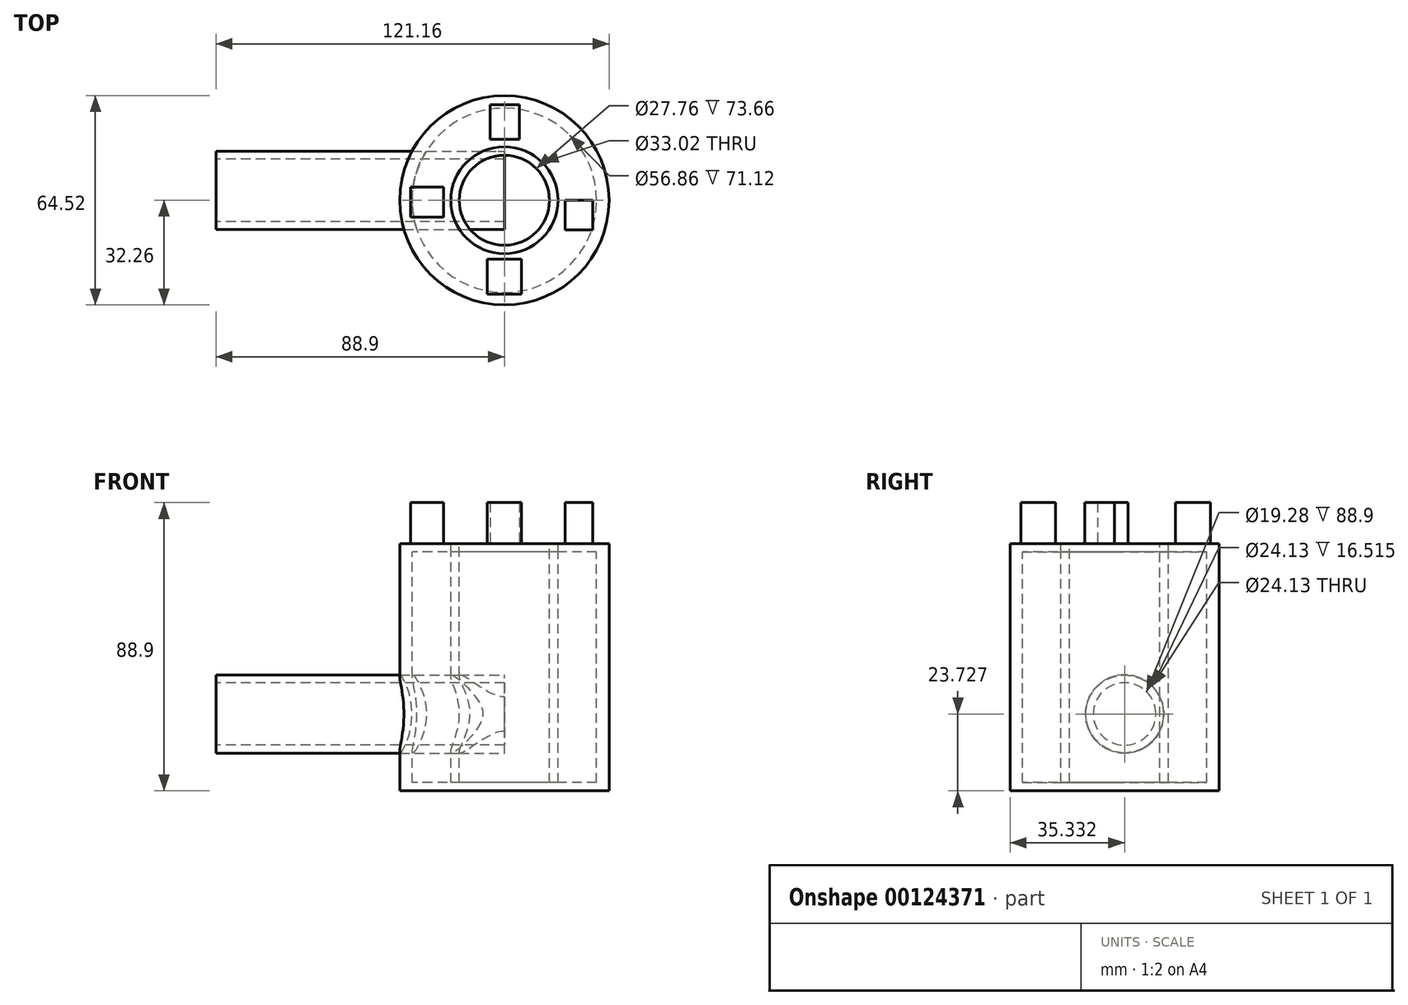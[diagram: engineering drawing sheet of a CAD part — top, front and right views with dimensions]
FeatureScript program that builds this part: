
annotation { "Feature Type Name" : "Feature", "Feature Type Description" : "" }
export const myFeature = defineFeature(function(context is Context, id is Id, definition is map)
    precondition{}
    {
        {
            var Q0;
            Q0=qCreatedBy(makeId("Top.planeOp"),FACE);
            var sketch = newSketch(context, id + "F0", { "sketchPlane" : qUnion([Q0])});
            skCircle(sketch, "E0", {"center": v(0, 0) * mm, "radius": 32.26 * mm});
            skSolve(sketch);
        }
        {
            var Q0;
            Q0=makeQuery(id+"F0.imprint","IMPRINT",FACE,{"disambiguationData":[TD([[makeQuery(id+"F0.imprint","IMPRINT",EDGE,{"derivedFrom":sQuery(id+"F0.wireOp",EDGE,"E0")}),1.0]])]});
            extrude(context, id + "F1", {"entities" : qUnion([Q0]), "depth" : 76.2 * mm});
        }
        {
            var Q0;
            Q0=makeQuery(id+"F1.opExtrude","CAP_FACE",FACE,{"disambiguationData":[OSD([sQuery(id+"F0.wireOp",EDGE,"E0")])],"isStart":false});
            var sketch = newSketch(context, id + "F2", { "sketchPlane" : qUnion([Q0])});
            skCircle(sketch, "E1", {"center": v(0, 0) * mm, "radius": 28.43 * mm});
            skSolve(sketch);
        }
        {
            var Q0;
            Q0=makeQuery(id+"F2.imprint","IMPRINT",FACE,{"disambiguationData":[TD([[makeQuery(id+"F2.imprint","IMPRINT",EDGE,{"derivedFrom":sQuery(id+"F2.wireOp",EDGE,"E1")}),1.0]])]});
            extrude(context, id + "F3", {"entities" : qUnion([Q0]), "operationType" : NewBodyOperationType.REMOVE, "oppositeDirection" : true, "depth" : 73.66 * mm});
        }
        {
            var Q0;
            Q0=makeQuery(id+"F1.opExtrude","CAP_FACE",FACE,{"disambiguationData":[OSD([sQuery(id+"F0.wireOp",EDGE,"E0")])],"isStart":false});
            var sketch = newSketch(context, id + "F4", { "sketchPlane" : qUnion([Q0])});
            skCircle(sketch, "E2", {"center": v(0, 0) * mm, "radius": 16.51 * mm});
            skCircle(sketch, "E3", {"center": v(0, 0) * mm, "radius": 28.68 * mm});
            skSolve(sketch);
        }
        {
            var Q0;
            Q0=makeQuery(id+"F4.imprint","IMPRINT",FACE,{"disambiguationData":[TD([[makeQuery(id+"F4.imprint","IMPRINT",EDGE,{"derivedFrom":sQuery(id+"F4.wireOp",EDGE,"E2")}),-1.0]])]});
            extrude(context, id + "F5", {"entities" : qUnion([Q0]), "operationType" : NewBodyOperationType.ADD, "oppositeDirection" : true, "depth" : 2.54 * mm});
        }
        {
            var Q0;
            Q0=makeQuery(id+"F5.boolean.opBoolean","MERGE",FACE,{"derivedFrom":[makeQuery(id+"F1.opExtrude","CAP_FACE",FACE,{"disambiguationData":[OSD([sQuery(id+"F0.wireOp",EDGE,"E0")])],"isStart":false}),makeQuery(id+"F5.opExtrude","CAP_FACE",FACE,{"disambiguationData":[OSD([sQuery(id+"F2.wireOp",EDGE,"E1"),sQuery(id+"F4.wireOp",EDGE,"E2")])],"isStart":true})]});
            var sketch = newSketch(context, id + "F6", { "sketchPlane" : qUnion([Q0])});
            skCircle(sketch, "E4", {"center": v(0, 0) * mm, "radius": 16.51 * mm});
            skSolve(sketch);
        }
        {
            var Q0;
            Q0 = qSketchRegion(id + "F6", true);
            extrude(context, id + "F7", {"entities" : qUnion([Q0]), "oppositeDirection" : true, "depth" : 73.66 * mm});
        }
        {
            var Q0;
            Q0=makeQuery(id+"F7.opExtrude","CAP_FACE",FACE,{"disambiguationData":[OSD([sQuery(id+"F6.wireOp",EDGE,"E4")])],"isStart":true});
            var sketch = newSketch(context, id + "F8", { "sketchPlane" : qUnion([Q0])});
            skCircle(sketch, "E5", {"center": v(0, 0) * mm, "radius": 13.88 * mm});
            skSolve(sketch);
        }
        {
            var Q0;
            Q0 = qSketchRegion(id + "F8", true);
            extrude(context, id + "F9", {"entities" : qUnion([Q0]), "operationType" : NewBodyOperationType.REMOVE, "oppositeDirection" : true, "depth" : 73.66 * mm});
        }
        {
            var Q0;
            Q0=qCreatedBy(makeId("Right.planeOp"),FACE);
            var sketch = newSketch(context, id + "F10", { "sketchPlane" : qUnion([Q0])});
            skCircle(sketch, "E6", {"center": v(3.07, 23.73) * mm, "radius": 12.07 * mm});
            skSolve(sketch);
        }
        {
            var Q0;
            Q0 = qSketchRegion(id + "F10", true);
            extrude(context, id + "F11", {"entities" : qUnion([Q0]), "operationType" : NewBodyOperationType.REMOVE, "oppositeDirection" : true, "depth" : 88.3 * mm});
        }
        {
            var Q0;
            Q0=makeQuery(id+"F5.boolean.opBoolean","MERGE",FACE,{"derivedFrom":[makeQuery(id+"F1.opExtrude","CAP_FACE",FACE,{"disambiguationData":[OSD([sQuery(id+"F0.wireOp",EDGE,"E0")])],"isStart":false}),makeQuery(id+"F5.opExtrude","CAP_FACE",FACE,{"disambiguationData":[OSD([sQuery(id+"F2.wireOp",EDGE,"E1"),sQuery(id+"F4.wireOp",EDGE,"E2")])],"isStart":true})]});
            var sketch = newSketch(context, id + "F12", { "sketchPlane" : qUnion([Q0])});
            skLineSegment(sketch, "E7.bottom", {"start": v(-4.37, 29.5) * mm, "end": v(4.66, 29.5) * mm});
            skLineSegment(sketch, "E7.top", {"start": v(-4.37, 18.77) * mm, "end": v(4.66, 18.77) * mm});
            skLineSegment(sketch, "E7.left", {"start": v(-4.37, 29.5) * mm, "end": v(-4.37, 18.77) * mm});
            skLineSegment(sketch, "E7.right", {"start": v(4.66, 29.5) * mm, "end": v(4.66, 18.77) * mm});
            skLineSegment(sketch, "E8.bottom", {"start": v(18.77, 0) * mm, "end": v(27.23, 0) * mm});
            skLineSegment(sketch, "E8.top", {"start": v(18.77, -9.17) * mm, "end": v(27.23, -9.17) * mm});
            skLineSegment(sketch, "E8.left", {"start": v(18.77, 0) * mm, "end": v(18.77, -9.17) * mm});
            skLineSegment(sketch, "E8.right", {"start": v(27.23, 0) * mm, "end": v(27.23, -9.17) * mm});
            skLineSegment(sketch, "E9.bottom", {"start": v(-5.22, -18.2) * mm, "end": v(5.22, -18.2) * mm});
            skLineSegment(sketch, "E9.top", {"start": v(-5.22, -28.93) * mm, "end": v(5.22, -28.93) * mm});
            skLineSegment(sketch, "E9.left", {"start": v(-5.22, -18.2) * mm, "end": v(-5.22, -28.93) * mm});
            skLineSegment(sketch, "E9.right", {"start": v(5.22, -18.2) * mm, "end": v(5.22, -28.93) * mm});
            skLineSegment(sketch, "E10.bottom", {"start": v(-28.93, 4.1) * mm, "end": v(-18.77, 4.1) * mm});
            skLineSegment(sketch, "E10.top", {"start": v(-28.93, -5.22) * mm, "end": v(-18.77, -5.22) * mm});
            skLineSegment(sketch, "E10.left", {"start": v(-28.93, 4.1) * mm, "end": v(-28.93, -5.22) * mm});
            skLineSegment(sketch, "E10.right", {"start": v(-18.77, 4.1) * mm, "end": v(-18.77, -5.22) * mm});
            skSolve(sketch);
        }
        {
            var Q0;
            Q0 = qSketchRegion(id + "F12", true);
            extrude(context, id + "F13", {"entities" : qUnion([Q0]), "operationType" : NewBodyOperationType.ADD, "depth" : 12.7 * mm});
        }
        {
            var Q0;
            Q0 = qSketchRegion(id + "F10", true);
            extrude(context, id + "F14", {"entities" : qUnion([Q0]), "oppositeDirection" : true, "depth" : 88.9 * mm});
        }
        {
            var Q0;
            Q0=makeQuery(id+"F14.opExtrude","CAP_FACE",FACE,{"disambiguationData":[OSD([sQuery(id+"F10.wireOp",EDGE,"E6")])],"isStart":false});
            var sketch = newSketch(context, id + "F15", { "sketchPlane" : qUnion([Q0])});
            skCircle(sketch, "E11", {"center": v(-3.07, 23.73) * mm, "radius": 9.64 * mm});
            skSolve(sketch);
        }
        {
            var Q0;
            Q0 = qSketchRegion(id + "F15", true);
            extrude(context, id + "F16", {"entities" : qUnion([Q0]), "operationType" : NewBodyOperationType.REMOVE, "oppositeDirection" : true, "depth" : 88.9 * mm});
        }
    });
